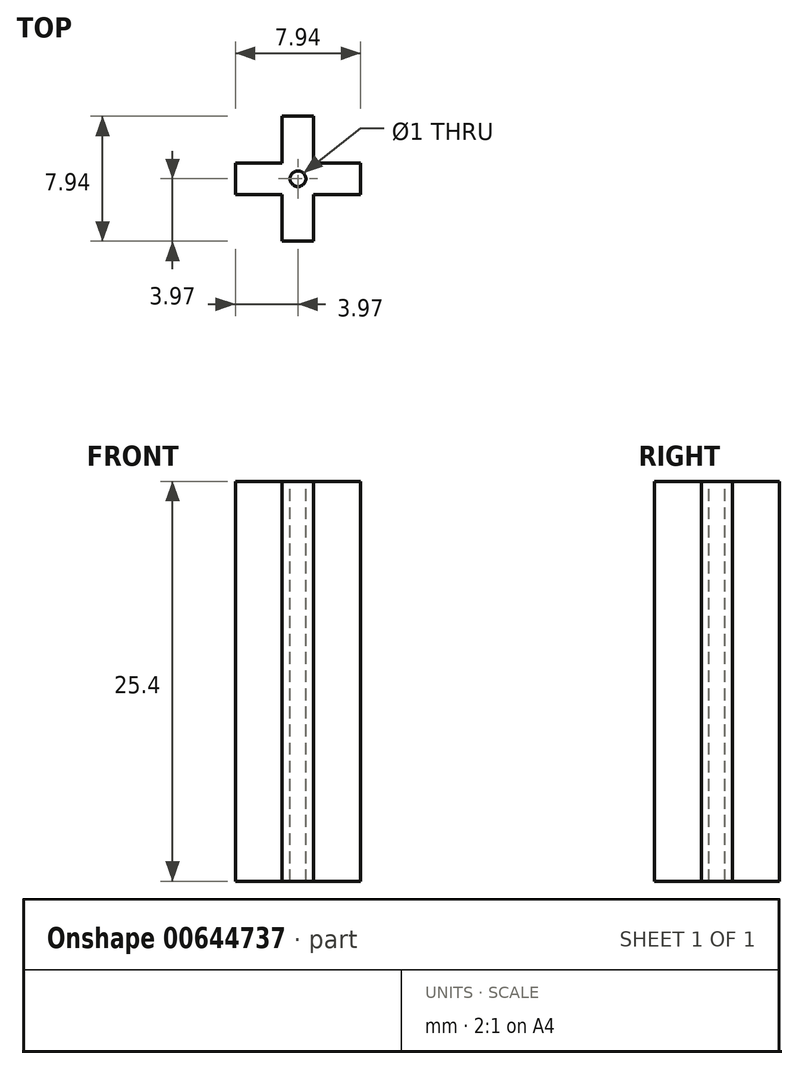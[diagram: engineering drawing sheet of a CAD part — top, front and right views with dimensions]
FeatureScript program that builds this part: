
annotation { "Feature Type Name" : "Feature", "Feature Type Description" : "" }
export const myFeature = defineFeature(function(context is Context, id is Id, definition is map)
    precondition{}
    {
        {
            var Q0;
            Q0=qCreatedBy(makeId("Top.planeOp"),FACE);
            var sketch = newSketch(context, id + "F0", { "sketchPlane" : qUnion([Q0])});
            skLineSegment(sketch, "E0.bottom", {"start": v(1, -3.97) * mm, "end": v(-1, -3.97) * mm});
            skLineSegment(sketch, "E0.top", {"start": v(1, 3.97) * mm, "end": v(-1, 3.97) * mm});
            skLineSegment(sketch, "E0.left", {"start": v(1, -3.97) * mm, "end": v(1, 3.97) * mm});
            skLineSegment(sketch, "E0.right", {"start": v(-1, -3.97) * mm, "end": v(-1, 3.97) * mm});
            skPoint(sketch, "E0.middle", {"position": v(0, 0) * mm});
            skLineSegment(sketch, "E1.bottom", {"start": v(3.97, -1) * mm, "end": v(-3.97, -1) * mm});
            skLineSegment(sketch, "E1.top", {"start": v(3.97, 1) * mm, "end": v(-3.97, 1) * mm});
            skLineSegment(sketch, "E1.left", {"start": v(3.97, -1) * mm, "end": v(3.97, 1) * mm});
            skLineSegment(sketch, "E1.right", {"start": v(-3.97, -1) * mm, "end": v(-3.97, 1) * mm});
            skPoint(sketch, "E2", {"position": v(1, -1) * mm});
            skPoint(sketch, "E3", {"position": v(1, 1) * mm});
            skPoint(sketch, "E3.positionSnap0", {"position": v(1, 0) * mm});
            skPoint(sketch, "E4", {"position": v(-1, 1) * mm});
            skPoint(sketch, "E5", {"position": v(-1, -1) * mm});
            skPoint(sketch, "E5.positionSnap0", {"position": v(0, -1) * mm});
            skSolve(sketch);
        }
        {
            var Q0;
            Q0 = qSketchRegion(id + "F0", true);
            extrude(context, id + "F1", {"entities" : qUnion([Q0]), "depth" : 25.4 * mm, "offsetDistance" : 25.4 * mm});
        }
        {
            var Q0;
            Q0=makeQuery(id+"F1.opExtrude","CAP_FACE",FACE,{"disambiguationData":[OSD([sQuery(id+"F0.wireOp",EDGE,"E0.bottom"),sQuery(id+"F0.wireOp",EDGE,"E0.top"),sQuery(id+"F0.wireOp",EDGE,"E0.left"),sQuery(id+"F0.wireOp",EDGE,"E0.right"),sQuery(id+"F0.wireOp",EDGE,"E1.bottom"),sQuery(id+"F0.wireOp",EDGE,"E1.top"),sQuery(id+"F0.wireOp",EDGE,"E1.left"),sQuery(id+"F0.wireOp",EDGE,"E1.right")])],"isStart":false});
            var sketch = newSketch(context, id + "F2", { "sketchPlane" : qUnion([Q0])});
            skCircle(sketch, "E6", {"center": v(0, 0) * mm, "radius": 4.1 * mm});
            skSolve(sketch);
        }
        {
            var Q0;
            {var subQ11=sQuery(id+"F0.wireOp",EDGE,"E0.bottom");Q0=makeQuery(id+"F2.imprint","IMPRINT",FACE,{"disambiguationData":[TD([[makeQuery(id+"F2.imprint","IMPRINT",EDGE,{"derivedFrom":makeQuery(id+"F1.opExtrude","CAP_EDGE",EDGE,{"disambiguationData":[OSD([subQ11])],"isStart":false})}),-1.0]])]});}
            var sketch = newSketch(context, id + "F3", { "sketchPlane" : qUnion([Q0])});
            skCircle(sketch, "E7", {"center": v(0, 0) * mm, "radius": 0.5 * mm});
            skSolve(sketch);
        }
        {
            var Q0;
            Q0=makeQuery(id+"F3.imprint","IMPRINT",FACE,{"disambiguationData":[TD([[makeQuery(id+"F3.imprint","IMPRINT",EDGE,{"derivedFrom":sQuery(id+"F3.wireOp",EDGE,"E7")}),1.0]])]});
            extrude(context, id + "F4", {"entities" : qUnion([Q0]), "operationType" : NewBodyOperationType.REMOVE, "endBound" : BoundingType.THROUGH_ALL, "oppositeDirection" : true, "depth" : 25 * mm, "offsetDistance" : 25 * mm});
        }
    });
